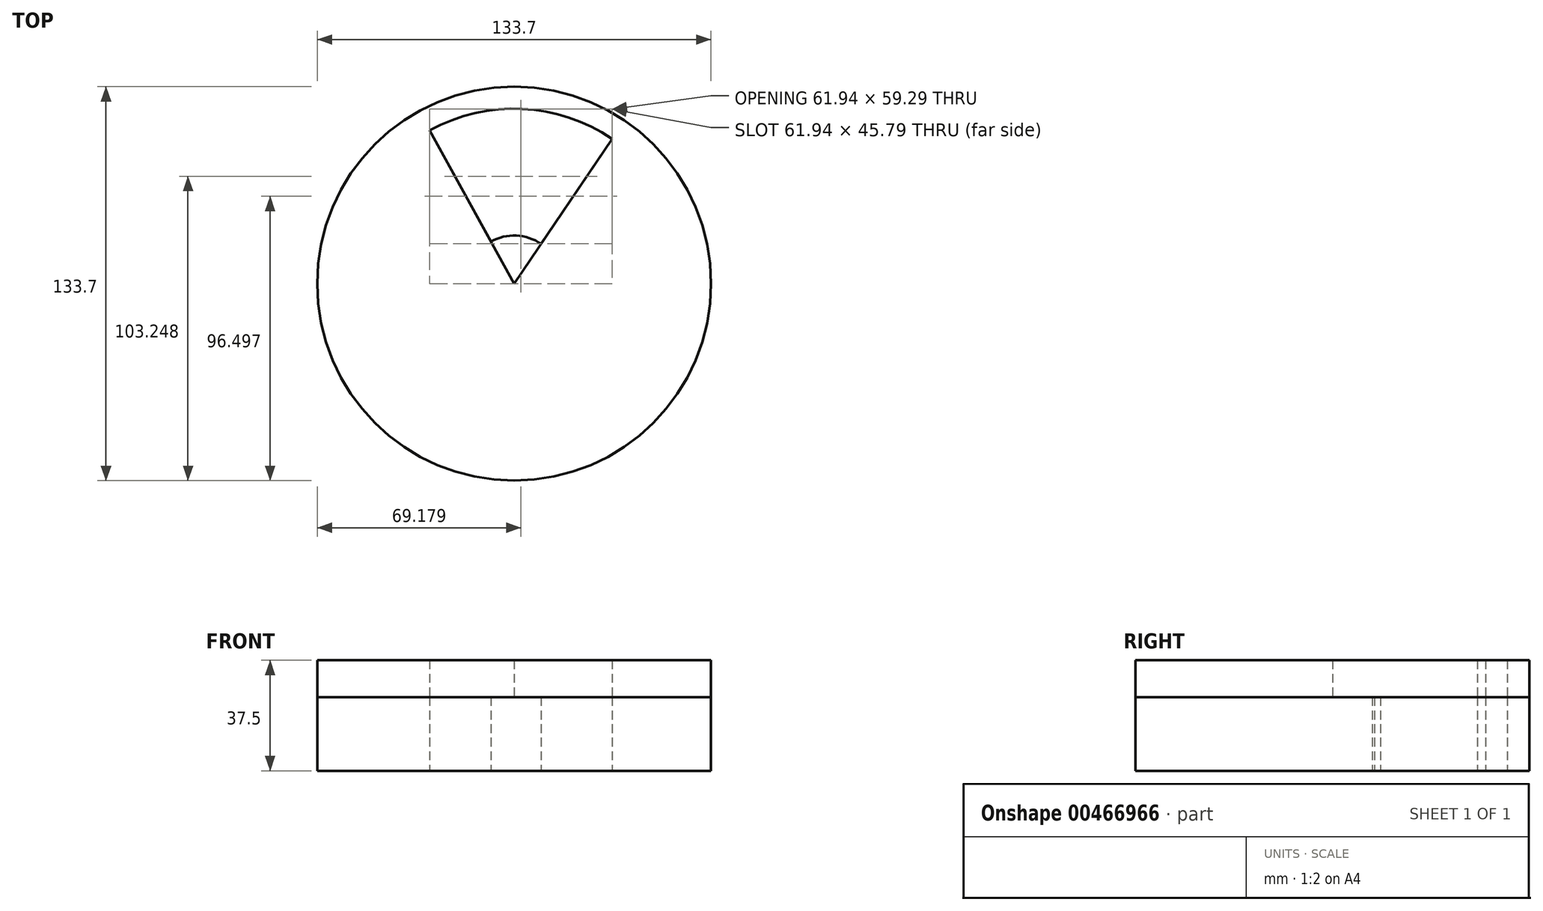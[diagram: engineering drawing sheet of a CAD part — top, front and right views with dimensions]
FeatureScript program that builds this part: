
annotation { "Feature Type Name" : "Feature", "Feature Type Description" : "" }
export const myFeature = defineFeature(function(context is Context, id is Id, definition is map)
    precondition{}
    {
        {
            var Q0;
            Q0=qCreatedBy(makeId("Top.planeOp"),FACE);
            var sketch = newSketch(context, id + "F0", { "sketchPlane" : qUnion([Q0])});
            skCircle(sketch, "E0", {"center": v(0, 0) * mm, "radius": 66.85 * mm});
            skCircle(sketch, "E1", {"center": v(0, 0) * mm, "radius": 59.36 * mm});
            skCircle(sketch, "E2", {"center": v(0, 0) * mm, "radius": 16.3 * mm});
            skLineSegment(sketch, "E3", {"start": v(0, 0) * mm, "end": v(-7.87, 14.29) * mm});
            skLineSegment(sketch, "E4", {"start": v(-7.87, 14.29) * mm, "end": v(-28.64, 52) * mm});
            skLineSegment(sketch, "E5", {"start": v(0, 0) * mm, "end": v(9.15, 13.5) * mm});
            skLineSegment(sketch, "E6", {"start": v(9.15, 13.5) * mm, "end": v(33.3, 49.14) * mm});
            skSolve(sketch);
        }
        {
            var Q0;
            Q0=makeQuery(id+"F0.imprint","IMPRINT",FACE,{"disambiguationData":[TD([[makeQuery(id+"F0.imprint","IMPRINT",EDGE,{"derivedFrom":sQuery(id+"F0.wireOp",EDGE,"E0")}),1.0]])]});
            var Q1;
            {var subQ0=sQuery(id+"F0.wireOp",EDGE,"E4");Q1=makeQuery(id+"F0.imprint","IMPRINT",FACE,{"disambiguationData":[TD([[makeQuery(id+"F0.imprint","IMPRINT",EDGE,{"derivedFrom":subQ0}),1.0]])]});}
            var Q2;
            {var subQ0=sQuery(id+"F0.wireOp",EDGE,"E3");Q2=makeQuery(id+"F0.imprint","IMPRINT",FACE,{"disambiguationData":[TD([[makeQuery(id+"F0.imprint","IMPRINT",EDGE,{"derivedFrom":subQ0}),1.0]])]});}
            var Q3;
            {var subQ0=sQuery(id+"F0.wireOp",EDGE,"E3");Q3=makeQuery(id+"F0.imprint","IMPRINT",FACE,{"disambiguationData":[TD([[makeQuery(id+"F0.imprint","IMPRINT",EDGE,{"derivedFrom":subQ0}),-1.0]])]});}
            extrude(context, id + "F1", {"entities" : qUnion([Q0, Q1, Q2, Q3]), "endBound" : BoundingType.SYMMETRIC, "depth" : 25 * mm});
        }
        {
            var Q0;
            {var subQ0=sQuery(id+"F0.wireOp",EDGE,"E4");Q0=makeQuery(id+"F0.imprint","IMPRINT",FACE,{"disambiguationData":[TD([[makeQuery(id+"F0.imprint","IMPRINT",EDGE,{"derivedFrom":subQ0}),1.0]])]});}
            var Q1;
            Q1=makeQuery(id+"F0.imprint","IMPRINT",FACE,{"disambiguationData":[TD([[makeQuery(id+"F0.imprint","IMPRINT",EDGE,{"derivedFrom":sQuery(id+"F0.wireOp",EDGE,"E0")}),1.0]])]});
            var Q2;
            {var subQ0=sQuery(id+"F0.wireOp",EDGE,"E3");Q2=makeQuery(id+"F0.imprint","IMPRINT",FACE,{"disambiguationData":[TD([[makeQuery(id+"F0.imprint","IMPRINT",EDGE,{"derivedFrom":subQ0}),1.0]])]});}
            var Q3;
            Q3=makeQuery(id+"F1.opExtrude","CAP_FACE",FACE,{"disambiguationData":[OSD([sQuery(id+"F0.wireOp",EDGE,"E0"),sQuery(id+"F0.wireOp",EDGE,"E1"),sQuery(id+"F0.wireOp",EDGE,"E2"),sQuery(id+"F0.wireOp",EDGE,"E4"),sQuery(id+"F0.wireOp",EDGE,"E6")])],"isStart":false});
            extrude(context, id + "F2", {"entities" : qUnion([Q0, Q1, Q2]), "depth" : 25 * mm, "hasSecondDirection" : true, "secondDirectionBound" : SecondDirectionBoundingType.UP_TO_SURFACE, "secondDirectionOppositeDirection" : false, "secondDirectionBoundEntityFace" : qUnion([Q3]), "secondDirectionDepth" : 25 * mm});
        }
    });
